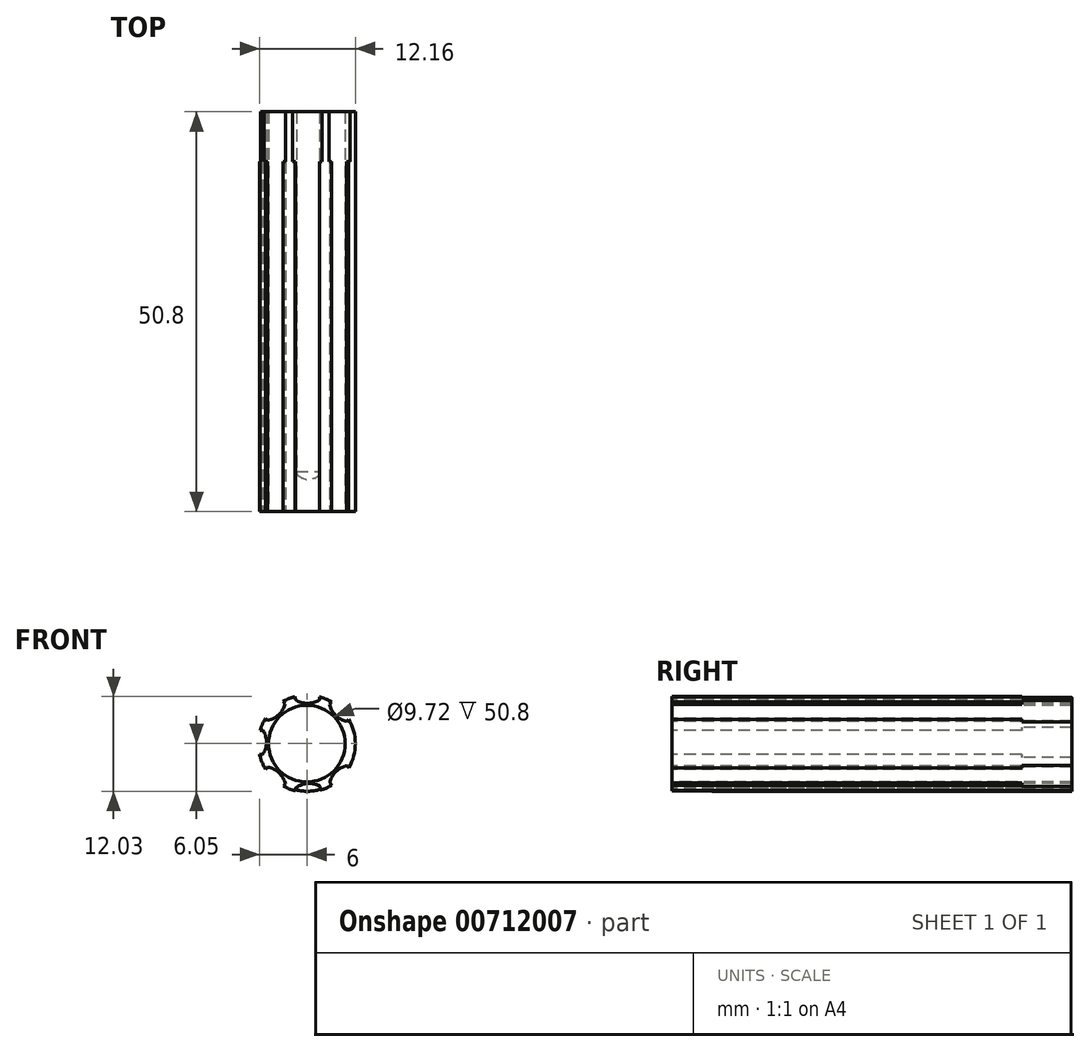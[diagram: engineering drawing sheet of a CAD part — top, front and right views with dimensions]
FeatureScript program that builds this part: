
annotation { "Feature Type Name" : "Feature", "Feature Type Description" : "" }
export const myFeature = defineFeature(function(context is Context, id is Id, definition is map)
    precondition{}
    {
        {
            var Q0;
            Q0=qCreatedBy(makeId("Front.planeOp"),FACE);
            var sketch = newSketch(context, id + "F0", { "sketchPlane" : qUnion([Q0])});
            skCircle(sketch, "E0", {"center": v(0, 0) * mm, "radius": 4.86 * mm});
            skArc(sketch, "E1", {"start": v(-5.91, -1.74) * mm, "mid": v(-5.12, 0.13) * mm, "end": v(-5.81, 2.05) * mm});
            skLineSegment(sketch, "E2.0", {"start": v(-5.61, -1.38) * mm, "end": v(-6, -1.4) * mm});
            skLineSegment(sketch, "E2.3", {"start": v(-5.92, 1.7) * mm, "end": v(-5.54, 1.67) * mm});
            skLineSegment(sketch, "E2.4", {"start": v(-5.61, -1.38) * mm, "end": v(-5.61, -1.38) * mm});
            skArc(sketch, "E3.1.0", {"start": v(-5.43, 2.9) * mm, "mid": v(-3.56, 3.7) * mm, "end": v(-2.7, 5.54) * mm});
            skLineSegment(sketch, "E3.1.1", {"start": v(-3.03, 5.37) * mm, "end": v(-2.77, 5.08) * mm});
            skLineSegment(sketch, "E3.1.2", {"start": v(-4.97, 2.96) * mm, "end": v(-5.25, 3.22) * mm});
            skArc(sketch, "E3.2.0", {"start": v(-1.83, 5.89) * mm, "mid": v(0.06, 5.12) * mm, "end": v(1.96, 5.84) * mm});
            skLineSegment(sketch, "E3.2.1", {"start": v(1.6, 5.95) * mm, "end": v(1.59, 5.56) * mm});
            skLineSegment(sketch, "E3.2.2", {"start": v(-1.46, 5.6) * mm, "end": v(-1.48, 5.98) * mm});
            skArc(sketch, "E3.3.0", {"start": v(2.83, 5.48) * mm, "mid": v(3.64, 3.61) * mm, "end": v(5.5, 2.79) * mm});
            skLineSegment(sketch, "E3.3.1", {"start": v(5.32, 3.1) * mm, "end": v(5.03, 2.85) * mm});
            skLineSegment(sketch, "E3.3.2", {"start": v(2.88, 5.01) * mm, "end": v(3.14, 5.3) * mm});
            skArc(sketch, "E3.5.0", {"start": v(5.52, -2.74) * mm, "mid": v(3.66, -3.58) * mm, "end": v(2.87, -5.46) * mm});
            skLineSegment(sketch, "E3.5.1", {"start": v(3.19, -5.27) * mm, "end": v(2.92, -5) * mm});
            skLineSegment(sketch, "E3.5.2", {"start": v(5.05, -2.8) * mm, "end": v(5.35, -3.06) * mm});
            skLineSegment(sketch, "E3.anchor1", {"start": v(0, 0) * mm, "end": v(-5.91, -1.74) * mm, "construction": true});
            skLineSegment(sketch, "E3.anchor2", {"start": v(0, 0) * mm, "end": v(-2.66, -5.56) * mm, "construction": true});
            skArc(sketch, "E4.2.6.0", {"start": v(2.13, -5.74) * mm, "mid": v(0.15, -5.04) * mm, "end": v(-1.76, -5.9) * mm});
            skLineSegment(sketch, "E4.4.6.0", {"start": v(-1.43, -6) * mm, "end": v(-1.42, -5.6) * mm});
            skLineSegment(sketch, "E4.7.6.0", {"start": v(1.7, -5.43) * mm, "end": v(1.66, -5.94) * mm});
            skArc(sketch, "E4.2.7.0", {"start": v(-2.66, -5.56) * mm, "mid": v(-3.53, -3.72) * mm, "end": v(-5.41, -2.95) * mm});
            skLineSegment(sketch, "E4.4.7.0", {"start": v(-5.23, -3.27) * mm, "end": v(-4.95, -3) * mm});
            skLineSegment(sketch, "E4.7.7.0", {"start": v(-2.73, -5.1) * mm, "end": v(-2.98, -5.4) * mm});
            skLineSegment(sketch, "E5.bottom", {"start": v(2.78, 0.93) * mm, "end": v(4.77, 0.93) * mm, "construction": true});
            skLineSegment(sketch, "E5.top", {"start": v(2.78, -0.8) * mm, "end": v(4.8, -0.8) * mm, "construction": true});
            skLineSegment(sketch, "E5.left", {"start": v(2.78, 0.93) * mm, "end": v(2.78, -0.8) * mm, "construction": true});
            skLineSegment(sketch, "E5.right", {"start": v(7.6, 0.93) * mm, "end": v(7.6, -0.8) * mm, "construction": true});
            skLineSegment(sketch, "E6.trimOffspring", {"start": v(6.1, 0.93) * mm, "end": v(7.6, 0.93) * mm, "construction": true});
            skLineSegment(sketch, "E7.trimOffspring", {"start": v(6.11, -0.8) * mm, "end": v(7.6, -0.8) * mm, "construction": true});
            skArc(sketch, "E8", {"start": v(1.66, -5.94) * mm, "mid": v(-0.12, 6.16) * mm, "end": v(-1.43, -6) * mm});
            skArc(sketch, "E9", {"start": v(-1.33, -5.9) * mm, "mid": v(0.16, -6.04) * mm, "end": v(1.64, -5.83) * mm});
            skLineSegment(sketch, "E10", {"start": v(1.64, -5.83) * mm, "end": v(1.67, -5.43) * mm});
            skLineSegment(sketch, "E11", {"start": v(-1.33, -5.9) * mm, "end": v(-1.33, -5.6) * mm});
            skArc(sketch, "E12", {"start": v(1.67, -5.43) * mm, "mid": v(0.14, -5.05) * mm, "end": v(-1.33, -5.6) * mm});
            skSolve(sketch);
        }
        {
            var Q0;
            Q0=makeQuery(id+"F0.imprint","IMPRINT",FACE,{"disambiguationData":[TD([[makeQuery(id+"F0.imprint","IMPRINT",EDGE,{"derivedFrom":sQuery(id+"F0.wireOp",EDGE,"E0")}),-1.0]])]});
            extrude(context, id + "F1", {"entities" : qUnion([Q0]), "oppositeDirection" : true, "depth" : 25.4 * mm, "offsetDistance" : 25.4 * mm, "hasSecondDirection" : true, "secondDirectionOppositeDirection" : false, "secondDirectionDepth" : 25.4 * mm});
        }
        {
            var Q0;
            {var subQ3=sQuery(id+"F0.wireOp",EDGE,"E3.3.2");Q0=makeQuery(id+"F0.imprint","IMPRINT",FACE,{"disambiguationData":[TD([[makeQuery(id+"F0.imprint","IMPRINT",EDGE,{"derivedFrom":subQ3}),1.0]])]});}
            var Q1;
            {var subQ3=sQuery(id+"F0.wireOp",EDGE,"E3.2.1");Q1=makeQuery(id+"F0.imprint","IMPRINT",FACE,{"disambiguationData":[TD([[makeQuery(id+"F0.imprint","IMPRINT",EDGE,{"derivedFrom":subQ3}),1.0]])]});}
            var Q2;
            {var subQ3=sQuery(id+"F0.wireOp",EDGE,"E3.2.2");Q2=makeQuery(id+"F0.imprint","IMPRINT",FACE,{"disambiguationData":[TD([[makeQuery(id+"F0.imprint","IMPRINT",EDGE,{"derivedFrom":subQ3}),1.0]])]});}
            var Q3;
            {var subQ3=sQuery(id+"F0.wireOp",EDGE,"E3.1.1");Q3=makeQuery(id+"F0.imprint","IMPRINT",FACE,{"disambiguationData":[TD([[makeQuery(id+"F0.imprint","IMPRINT",EDGE,{"derivedFrom":subQ3}),1.0]])]});}
            var Q4;
            {var subQ3=sQuery(id+"F0.wireOp",EDGE,"E3.1.2");Q4=makeQuery(id+"F0.imprint","IMPRINT",FACE,{"disambiguationData":[TD([[makeQuery(id+"F0.imprint","IMPRINT",EDGE,{"derivedFrom":subQ3}),1.0]])]});}
            var Q5;
            {var subQ3=sQuery(id+"F0.wireOp",EDGE,"E2.3");Q5=makeQuery(id+"F0.imprint","IMPRINT",FACE,{"disambiguationData":[TD([[makeQuery(id+"F0.imprint","IMPRINT",EDGE,{"derivedFrom":subQ3}),1.0]])]});}
            var Q6;
            {var subQ3=sQuery(id+"F0.wireOp",EDGE,"E2.0");Q6=makeQuery(id+"F0.imprint","IMPRINT",FACE,{"disambiguationData":[TD([[makeQuery(id+"F0.imprint","IMPRINT",EDGE,{"derivedFrom":subQ3}),1.0]])]});}
            var Q7;
            {var subQ3=sQuery(id+"F0.wireOp",EDGE,"E3.3.1");Q7=makeQuery(id+"F0.imprint","IMPRINT",FACE,{"disambiguationData":[TD([[makeQuery(id+"F0.imprint","IMPRINT",EDGE,{"derivedFrom":subQ3}),1.0]])]});}
            var Q8;
            {var subQ3=sQuery(id+"F0.wireOp",EDGE,"E3.5.2");Q8=makeQuery(id+"F0.imprint","IMPRINT",FACE,{"disambiguationData":[TD([[makeQuery(id+"F0.imprint","IMPRINT",EDGE,{"derivedFrom":subQ3}),1.0]])]});}
            var Q9;
            {var subQ3=sQuery(id+"F0.wireOp",EDGE,"E3.5.1");Q9=makeQuery(id+"F0.imprint","IMPRINT",FACE,{"disambiguationData":[TD([[makeQuery(id+"F0.imprint","IMPRINT",EDGE,{"derivedFrom":subQ3}),1.0]])]});}
            var Q10;
            {var subQ3=sQuery(id+"F0.wireOp",EDGE,"E4.7.6.0");Q10=makeQuery(id+"F0.imprint","IMPRINT",FACE,{"disambiguationData":[TD([[makeQuery(id+"F0.imprint","IMPRINT",EDGE,{"derivedFrom":subQ3}),1.0]])]});}
            var Q11;
            {var subQ3=sQuery(id+"F0.wireOp",EDGE,"E4.4.6.0");Q11=makeQuery(id+"F0.imprint","IMPRINT",FACE,{"disambiguationData":[TD([[makeQuery(id+"F0.imprint","IMPRINT",EDGE,{"derivedFrom":subQ3}),1.0]])]});}
            var Q12;
            {var subQ3=sQuery(id+"F0.wireOp",EDGE,"E4.7.7.0");Q12=makeQuery(id+"F0.imprint","IMPRINT",FACE,{"disambiguationData":[TD([[makeQuery(id+"F0.imprint","IMPRINT",EDGE,{"derivedFrom":subQ3}),1.0]])]});}
            var Q13;
            {var subQ3=sQuery(id+"F0.wireOp",EDGE,"E4.4.7.0");Q13=makeQuery(id+"F0.imprint","IMPRINT",FACE,{"disambiguationData":[TD([[makeQuery(id+"F0.imprint","IMPRINT",EDGE,{"derivedFrom":subQ3}),1.0]])]});}
            var Q14;
            Q14=makeQuery(id+"F1.opExtrude","CAP_FACE",FACE,{"disambiguationData":[OSD([sQuery(id+"F0.wireOp",EDGE,"2tQNeWs4-3cw0-mdHs-wFZ3-JT7oUkEsEbXL"),sQuery(id+"F0.wireOp",EDGE,"E0"),sQuery(id+"F0.wireOp",EDGE,"E1"),sQuery(id+"F0.wireOp",EDGE,"E3.1.0"),sQuery(id+"F0.wireOp",EDGE,"E3.2.0"),sQuery(id+"F0.wireOp",EDGE,"E3.3.0"),sQuery(id+"F0.wireOp",EDGE,"E3.5.0"),sQuery(id+"F0.wireOp",EDGE,"E4.2.6.0"),sQuery(id+"F0.wireOp",EDGE,"E4.2.7.0")])],"isStart":false});
            var Q15;
            Q15=makeQuery(id+"F1.opExtrude","CAP_FACE",FACE,{"disambiguationData":[OSD([sQuery(id+"F0.wireOp",EDGE,"2tQNeWs4-3cw0-mdHs-wFZ3-JT7oUkEsEbXL"),sQuery(id+"F0.wireOp",EDGE,"E0"),sQuery(id+"F0.wireOp",EDGE,"E1"),sQuery(id+"F0.wireOp",EDGE,"E3.1.0"),sQuery(id+"F0.wireOp",EDGE,"E3.2.0"),sQuery(id+"F0.wireOp",EDGE,"E3.3.0"),sQuery(id+"F0.wireOp",EDGE,"E3.5.0"),sQuery(id+"F0.wireOp",EDGE,"E4.2.6.0"),sQuery(id+"F0.wireOp",EDGE,"E4.2.7.0")])],"isStart":true});
            extrude(context, id + "F2", {"entities" : qUnion([Q0, Q1, Q2, Q3, Q4, Q5, Q6, Q7, Q8, Q9, Q10, Q11, Q12, Q13]), "operationType" : NewBodyOperationType.ADD, "endBound" : BoundingType.UP_TO_SURFACE, "oppositeDirection" : true, "depth" : 11.43 * mm, "endBoundEntityFace" : qUnion([Q14]), "hasOffset" : true, "offsetDistance" : 6.35 * mm, "hasSecondDirection" : true, "secondDirectionBound" : SecondDirectionBoundingType.UP_TO_SURFACE, "secondDirectionOppositeDirection" : false, "secondDirectionDepth" : 34.54 * mm, "secondDirectionBoundEntityFace" : qUnion([Q15])});
        }
        {
            var Q0;
            Q0=makeQuery(id+"F0.imprint","IMPRINT",FACE,{"disambiguationData":[TD([[makeQuery(id+"F0.imprint","IMPRINT",EDGE,{"derivedFrom":sQuery(id+"F0.wireOp",EDGE,"E9")}),1.0]])]});
            extrude(context, id + "F3", {"entities" : qUnion([Q0]), "oppositeDirection" : true, "depth" : 25.4 * mm, "offsetDistance" : 25.4 * mm, "hasSecondDirection" : true, "secondDirectionOppositeDirection" : false, "secondDirectionDepth" : 25.4 * mm});
        }
        {
            var Q0;
            Q0=makeQuery(id+"F3.opExtrude","CAP_EDGE",EDGE,{"disambiguationData":[OSD([sQuery(id+"F0.wireOp",EDGE,"E9")])],"isStart":true});
            chamfer(context, id + "F4", {"entities" : qUnion([Q0]), "width" : 5.08 * mm, "tangentPropagation" : true});
        }
    });
